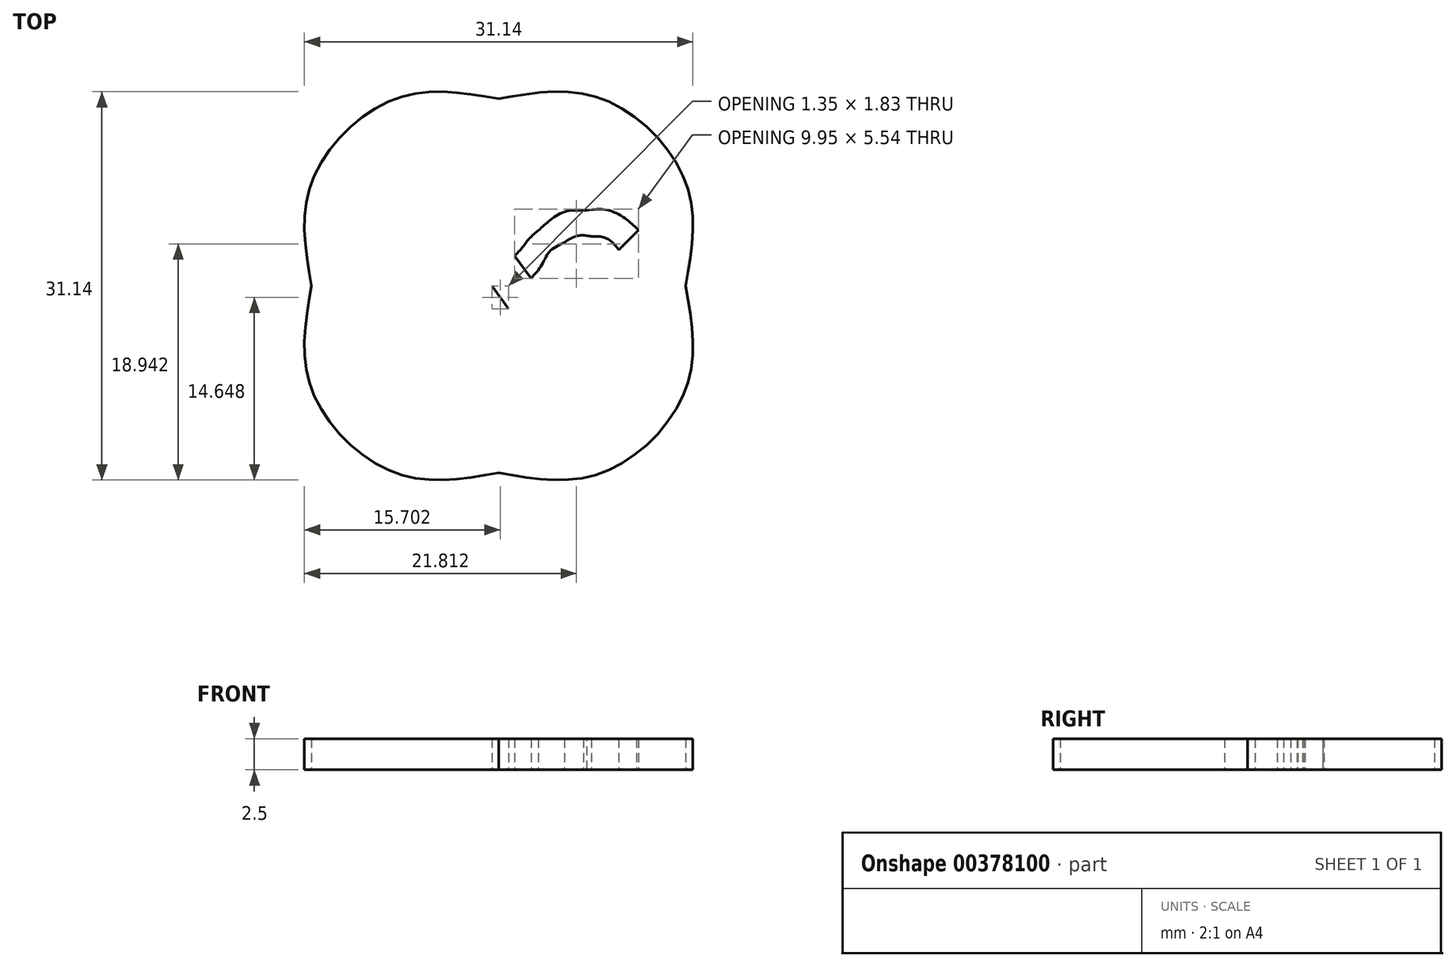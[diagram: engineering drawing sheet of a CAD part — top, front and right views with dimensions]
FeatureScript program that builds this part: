
annotation { "Feature Type Name" : "Feature", "Feature Type Description" : "" }
export const myFeature = defineFeature(function(context is Context, id is Id, definition is map)
    precondition{}
    {
        {
            var Q0;
            Q0=qCreatedBy(makeId("Top.planeOp"),FACE);
            var sketch = newSketch(context, id + "F0", { "sketchPlane" : qUnion([Q0])});
            skFitSpline(sketch, "E0", {"points": [v(0, 15) * mm, v(-8.28, 15) * mm, v(-15, 8.28) * mm, v(-15, 0) * mm]});
            skFitSpline(sketch, "E1", {"points": [v(-15, 0) * mm, v(-15, -8.28) * mm, v(-8.28, -15) * mm, v(0, -15) * mm]});
            skFitSpline(sketch, "E2", {"points": [v(0, -15) * mm, v(8.28, -15) * mm, v(15, -8.28) * mm, v(15, 0) * mm]});
            skFitSpline(sketch, "E3", {"points": [v(15, 0) * mm, v(15, 8.28) * mm, v(8.28, 15) * mm, v(0, 15) * mm]});
            skFitSpline(sketch, "E4", {"points": [v(-5.57, 6.07) * mm, v(-5.46, 6.07) * mm, v(-5.36, 6.06) * mm, v(-5.26, 6.05) * mm]});
            skFitSpline(sketch, "E5", {"points": [v(-5.26, 6.05) * mm, v(-3.72, 5.93) * mm, v(-2.51, 5.2) * mm, v(-1.65, 4.44) * mm]});
            skFitSpline(sketch, "E6", {"points": [v(-1.65, 4.44) * mm, v(-1.04, 3.9) * mm, v(-0.4, 3.16) * mm, v(0.2, 2.48) * mm]});
            skFitSpline(sketch, "E7", {"points": [v(0.2, 2.48) * mm, v(0.26, 2.42) * mm, v(0.34, 2.32) * mm, v(0.44, 2.2) * mm]});
            skFitSpline(sketch, "E8", {"points": [v(2.08, 0) * mm, v(2.08, 0) * mm, v(2.08, 0) * mm, v(2.08, 0) * mm]});
            skFitSpline(sketch, "E9", {"points": [v(2.08, 0) * mm, v(3.12, -1.31) * mm, v(4.03, -2.93) * mm, v(5.59, -3.67) * mm]});
            skFitSpline(sketch, "E10", {"points": [v(5.59, -3.67) * mm, v(5.9, -3.83) * mm, v(6.33, -3.95) * mm, v(6.73, -3.99) * mm]});
            skFitSpline(sketch, "E11", {"points": [v(6.73, -3.99) * mm, v(8.05, -4.1) * mm, v(9.01, -3.64) * mm, v(9.64, -2.91) * mm]});
            skLineSegment(sketch, "E12", {"start": v(0.44, 2.2) * mm, "end": v(2.08, 0) * mm});
            skLineSegment(sketch, "E13", {"start": v(2.08, 0) * mm, "end": v(0.44, 2.2) * mm});
            skFitSpline(sketch, "E14", {"points": [v(11.2, -4.47) * mm, v(10.89, -4.79) * mm, v(10.53, -5.06) * mm, v(10.11, -5.3) * mm]});
            skFitSpline(sketch, "E15", {"points": [v(10.11, -5.3) * mm, v(9.3, -5.74) * mm, v(8.28, -6.05) * mm, v(7.25, -6.07) * mm]});
            skFitSpline(sketch, "E16", {"points": [v(7.25, -6.07) * mm, v(4.46, -6.11) * mm, v(2.9, -4.28) * mm, v(1.56, -2.74) * mm]});
            skFitSpline(sketch, "E17", {"points": [v(1.56, -2.74) * mm, v(1.44, -2.61) * mm, v(1.3, -2.48) * mm, v(1.13, -2.28) * mm]});
            skFitSpline(sketch, "E18", {"points": [v(1.13, -2.28) * mm, v(1.07, -2.2) * mm, v(0.9, -1.95) * mm, v(0.8, -1.84) * mm]});
            skLineSegment(sketch, "E19", {"start": v(9.64, -2.91) * mm, "end": v(11.2, -4.47) * mm});
            skLineSegment(sketch, "E20", {"start": v(11.2, -4.47) * mm, "end": v(9.64, -2.91) * mm});
            skFitSpline(sketch, "E21", {"points": [v(-0.54, 0) * mm, v(-0.54, 0) * mm, v(-0.54, 0) * mm, v(-0.54, 0) * mm]});
            skFitSpline(sketch, "E22", {"points": [v(-0.54, 0) * mm, v(-1.45, 1.08) * mm, v(-2.46, 2.7) * mm, v(-3.73, 3.47) * mm]});
            skFitSpline(sketch, "E23", {"points": [v(-3.73, 3.47) * mm, v(-4.3, 3.82) * mm, v(-4.96, 4.04) * mm, v(-5.9, 3.97) * mm]});
            skFitSpline(sketch, "E24", {"points": [v(-5.9, 3.97) * mm, v(-7.94, 3.82) * mm, v(-8.98, 2.09) * mm, v(-9.06, 0.18) * mm]});
            skFitSpline(sketch, "E25", {"points": [v(-9.06, 0.18) * mm, v(-9.16, -1.97) * mm, v(-7.98, -4.22) * mm, v(-5.2, -3.99) * mm]});
            skFitSpline(sketch, "E26", {"points": [v(-5.2, -3.99) * mm, v(-4.8, -3.95) * mm, v(-4.37, -3.83) * mm, v(-4.05, -3.67) * mm]});
            skFitSpline(sketch, "E27", {"points": [v(-4.05, -3.67) * mm, v(-2.6, -2.97) * mm, v(-2.02, -1.9) * mm, v(-1.05, -0.63) * mm]});
            skLineSegment(sketch, "E28", {"start": v(0.8, -1.84) * mm, "end": v(-0.54, -0.01) * mm});
            skLineSegment(sketch, "E29", {"start": v(-0.54, -0.01) * mm, "end": v(-0.54, 0) * mm});
            skLineSegment(sketch, "E30", {"start": v(-0.54, 0) * mm, "end": v(0.8, -1.84) * mm});
            skFitSpline(sketch, "E31", {"points": [v(0.27, -2.4) * mm, v(0.19, -2.5) * mm, v(0.44, -2.23) * mm, v(-0.46, -3.25) * mm]});
            skFitSpline(sketch, "E32", {"points": [v(-0.46, -3.25) * mm, v(-1.36, -4.28) * mm, v(-2.92, -6.11) * mm, v(-5.71, -6.07) * mm]});
            skFitSpline(sketch, "E33", {"points": [v(-5.71, -6.07) * mm, v(-6.74, -6.05) * mm, v(-7.77, -5.74) * mm, v(-8.57, -5.3) * mm]});
            skFitSpline(sketch, "E34", {"points": [v(-8.57, -5.3) * mm, v(-10.16, -4.41) * mm, v(-11, -2.94) * mm, v(-11.18, -0.75) * mm]});
            skFitSpline(sketch, "E35", {"points": [v(-11.18, -0.75) * mm, v(-11.37, 1.64) * mm, v(-10.86, 3.47) * mm, v(-9.52, 4.62) * mm]});
            skFitSpline(sketch, "E36", {"points": [v(-9.52, 4.62) * mm, v(-8.6, 5.41) * mm, v(-7.11, 6.1) * mm, v(-5.57, 6.07) * mm]});
            skLineSegment(sketch, "E37", {"start": v(-1.05, -0.63) * mm, "end": v(0.27, -2.4) * mm});
            skLineSegment(sketch, "E38", {"start": v(0.27, -2.4) * mm, "end": v(-1.05, -0.63) * mm});
            skFitSpline(sketch, "E39", {"points": [v(7.1, 6.07) * mm, v(8.65, 6.1) * mm, v(10.13, 5.41) * mm, v(11.05, 4.62) * mm]});
            skFitSpline(sketch, "E40", {"points": [v(11.05, 4.62) * mm, v(11.1, 4.57) * mm, v(11.16, 4.52) * mm, v(11.22, 4.47) * mm]});
            skLineSegment(sketch, "E41", {"start": v(-5.57, 6.07) * mm, "end": v(-5.57, 6.07) * mm});
            skFitSpline(sketch, "E42", {"points": [v(9.63, 2.88) * mm, v(9.1, 3.5) * mm, v(8.38, 3.9) * mm, v(7.44, 3.97) * mm]});
            skFitSpline(sketch, "E43", {"points": [v(7.44, 3.97) * mm, v(6.5, 4.04) * mm, v(5.83, 3.82) * mm, v(5.26, 3.47) * mm]});
            skFitSpline(sketch, "E44", {"points": [v(5.26, 3.47) * mm, v(4.08, 2.75) * mm, v(3.46, 1.68) * mm, v(2.6, 0.6) * mm]});
            skLineSegment(sketch, "E45", {"start": v(11.22, 4.47) * mm, "end": v(9.63, 2.88) * mm});
            skLineSegment(sketch, "E46", {"start": v(9.63, 2.88) * mm, "end": v(11.22, 4.47) * mm});
            skFitSpline(sketch, "E47", {"points": [v(1.27, 2.39) * mm, v(1.9, 3.08) * mm, v(2.5, 3.83) * mm, v(3.18, 4.44) * mm]});
            skFitSpline(sketch, "E48", {"points": [v(3.18, 4.44) * mm, v(4.05, 5.2) * mm, v(5.26, 5.93) * mm, v(6.8, 6.05) * mm]});
            skFitSpline(sketch, "E49", {"points": [v(6.8, 6.05) * mm, v(6.9, 6.06) * mm, v(7, 6.07) * mm, v(7.1, 6.07) * mm]});
            skLineSegment(sketch, "E50", {"start": v(2.6, 0.6) * mm, "end": v(1.27, 2.39) * mm});
            skLineSegment(sketch, "E51", {"start": v(1.27, 2.39) * mm, "end": v(2.6, 0.6) * mm});
            skLineSegment(sketch, "E52", {"start": v(7.1, 6.07) * mm, "end": v(7.1, 6.07) * mm});
            skSolve(sketch);
        }
        {
            var Q0;
            Q0 = qSketchRegion(id + "F0", true);
            extrude(context, id + "F1", {"entities" : qUnion([Q0]), "depth" : 2.5 * mm});
        }
    });
